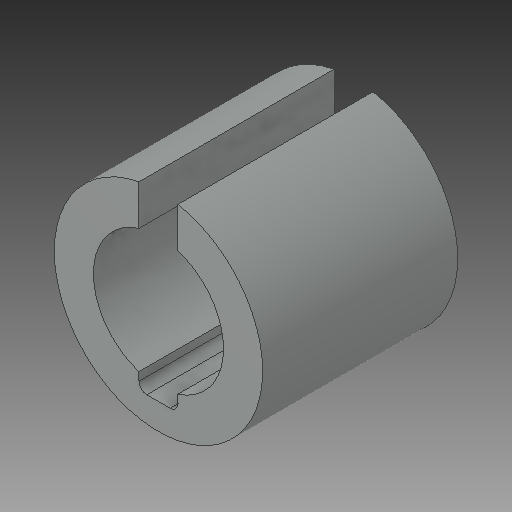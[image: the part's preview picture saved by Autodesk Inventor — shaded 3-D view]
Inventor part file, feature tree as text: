
AUTODESK INVENTOR PART (.ipt)
format: ipt  version: 2017 (Build 210142000, 142)  size: 118,784 bytes
history: native  units: in
note: dims shown in document units (in); Inventor stores cm internally (conversion verified against a paired STEP export)
features: fillet x1
ambient origin geometry x8: Origin, YZ Plane, XZ Plane, XY Plane, X Axis, Y Axis, Z Axis, Center Point
bodies: Solid1 (feature_tree)
feature tree (1):
  fillet  "Fillet1"  [1 undecoded]
note: 1 required parameter value undecoded (feature->parameter linkage not recoverable at this tier; creation-order binding heuristic only, values carry confidence <= 0.55)
